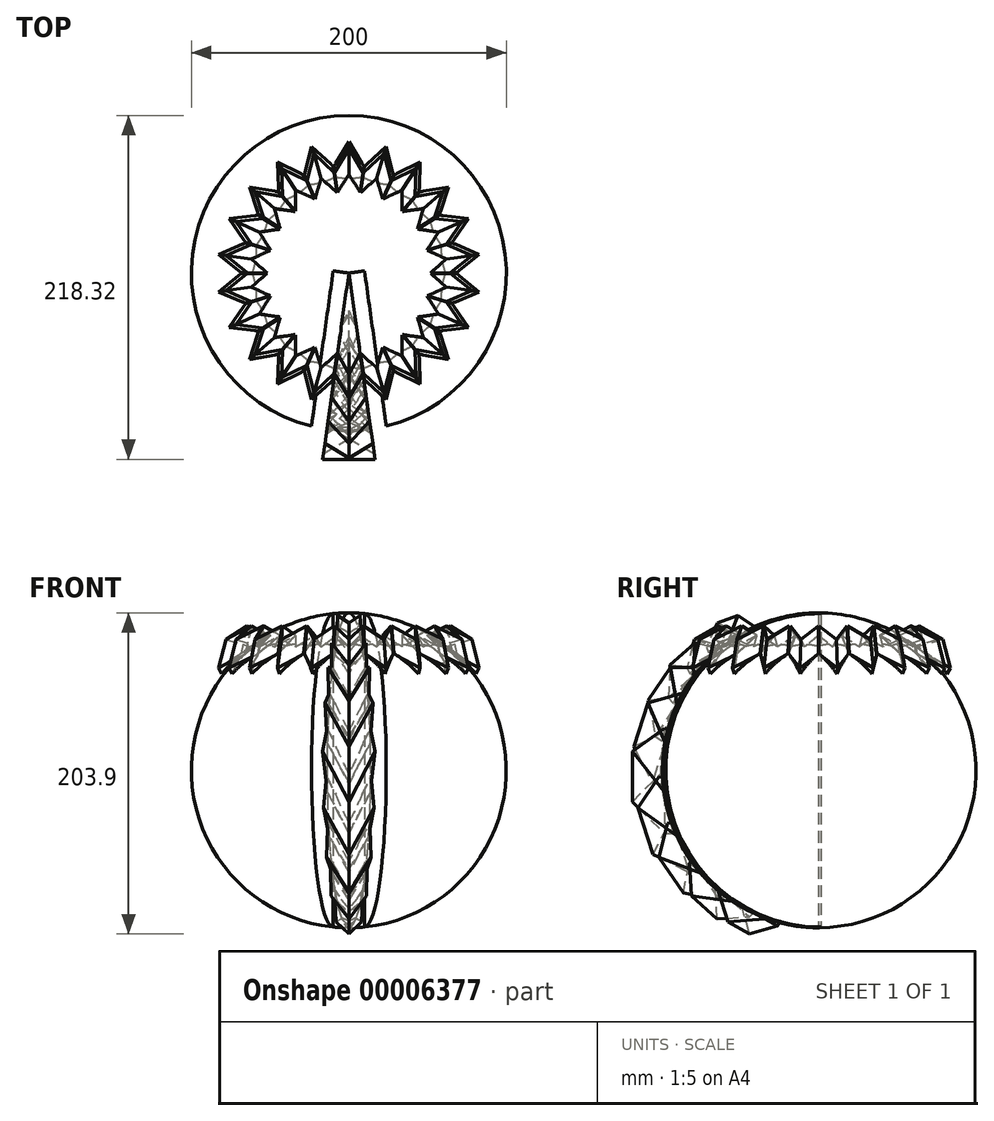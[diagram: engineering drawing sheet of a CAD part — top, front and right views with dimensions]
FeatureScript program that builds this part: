
annotation { "Feature Type Name" : "Feature", "Feature Type Description" : "" }
export const myFeature = defineFeature(function(context is Context, id is Id, definition is map)
    precondition{}
    {
        {
            var Q0;
            Q0=qCreatedBy(makeId("Front.planeOp"),FACE);
            var sketch = newSketch(context, id + "F0", { "sketchPlane" : qUnion([Q0])});
            skLineSegment(sketch, "E0", {"start": v(-20.82, 40) * mm, "end": v(0, 0) * mm});
            skLineSegment(sketch, "E1", {"start": v(0, 0) * mm, "end": v(20.82, 40) * mm});
            skLineSegment(sketch, "E2", {"start": v(-20.82, 40) * mm, "end": v(-20.82, 80) * mm});
            skLineSegment(sketch, "E3", {"start": v(-20.82, 80) * mm, "end": v(0, 40) * mm});
            skLineSegment(sketch, "E4", {"start": v(0, 40) * mm, "end": v(20.82, 80) * mm});
            skLineSegment(sketch, "E5", {"start": v(20.82, 80) * mm, "end": v(20.82, 40) * mm});
            skSolve(sketch);
        }
        {
            var Q0;
            Q0=makeQuery(id+"F0.imprint","IMPRINT",FACE,{"disambiguationData":[TD([[makeQuery(id+"F0.imprint","IMPRINT",EDGE,{"derivedFrom":sQuery(id+"F0.wireOp",EDGE,"E0")}),1.0]])]});
            extrude(context, id + "F1", {"entities" : qUnion([Q0]), "depth" : 120 * mm});
        }
        {
            var Q0;
            Q0=makeQuery(id+"F1.opExtrude","CAP_EDGE",EDGE,{"disambiguationData":[OSD([sQuery(id+"F0.wireOp",EDGE,"E3")])],"isStart":false});
            var Q1;
            Q1=makeQuery(id+"F1.opExtrude","CAP_EDGE",EDGE,{"disambiguationData":[OSD([sQuery(id+"F0.wireOp",EDGE,"E4")])],"isStart":false});
            var Q2;
            Q2=makeQuery(id+"F1.opExtrude","CAP_EDGE",EDGE,{"disambiguationData":[OSD([sQuery(id+"F0.wireOp",EDGE,"E1")])],"isStart":false});
            var Q3;
            Q3=makeQuery(id+"F1.opExtrude","CAP_EDGE",EDGE,{"disambiguationData":[OSD([sQuery(id+"F0.wireOp",EDGE,"E0")])],"isStart":false});
            chamfer(context, id + "F2", {"entities" : qUnion([Q0, Q1, Q2, Q3]), "chamferType" : ChamferType.TWO_OFFSETS, "width1" : 22 * mm, "oppositeDirection" : false, "width2" : 10 * mm, "tangentPropagation" : true});
        }
        {
            var Q0;
            Q0=qCreatedBy(makeId("Right.planeOp"),FACE);
            var sketch = newSketch(context, id + "F3", { "sketchPlane" : qUnion([Q0])});
            skArc(sketch, "E6", {"start": v(0, 140) * mm, "mid": v(-100, 40) * mm, "end": v(0, -60) * mm});
            skLineSegment(sketch, "E7", {"start": v(0, 140) * mm, "end": v(0, -60) * mm});
            skSolve(sketch);
        }
        {
            var Q0;
            Q0=makeQuery(id+"F3.imprint","IMPRINT",FACE,{"disambiguationData":[TD([[makeQuery(id+"F3.imprint","IMPRINT",EDGE,{"derivedFrom":sQuery(id+"F3.wireOp",EDGE,"E6")}),1.0]])]});
            var Q1;
            Q1=sQuery(id+"F3.wireOp",EDGE,"E7");
            revolve(context, id + "F4", {"entities" : qUnion([Q0]), "axis" : qUnion([Q1]), "revolveType" : RevolveType.FULL});
        }
        {
            var Q0;
            Q0=makeQuery(id+"F4.opRevolve","SWEPT_BODY",BODY,{"disambiguationData":[OSD([sQuery(id+"F3.wireOp",EDGE,"E6"),sQuery(id+"F3.wireOp",EDGE,"E7")])]});
            var Q1;
            Q1=makeQuery(id+"F1.opExtrude","SWEPT_BODY",BODY,{"disambiguationData":[OSD([sQuery(id+"F0.wireOp",EDGE,"E0"),sQuery(id+"F0.wireOp",EDGE,"E1"),sQuery(id+"F0.wireOp",EDGE,"E2"),sQuery(id+"F0.wireOp",EDGE,"E3"),sQuery(id+"F0.wireOp",EDGE,"E4"),sQuery(id+"F0.wireOp",EDGE,"E5")])]});
            booleanBodies(context, id + "F5", {"operationType" : BooleanOperationType.SUBTRACTION, "tools" : qUnion([Q0]), "targets" : qUnion([Q1]), "keepTools" : true});
        }
        {
            var Q0;
            Q0=makeQuery(id+"F1.opExtrude","SWEPT_BODY",BODY,{"disambiguationData":[OSD([sQuery(id+"F0.wireOp",EDGE,"E0"),sQuery(id+"F0.wireOp",EDGE,"E1"),sQuery(id+"F0.wireOp",EDGE,"E2"),sQuery(id+"F0.wireOp",EDGE,"E3"),sQuery(id+"F0.wireOp",EDGE,"E4"),sQuery(id+"F0.wireOp",EDGE,"E5")])]});
            var Q1;
            Q1=sQuery(id+"F3.wireOp",EDGE,"E6");
            circularPattern(context, id + "F6", {"entities" : qUnion([Q0]), "axis" : qUnion([Q1]), "angle" : 18 * degree, "instanceCount" : 2, "oppositeDirection" : true});
        }
        {
            var Q0;
            Q0=makeQuery(id+"F1.opExtrude","SWEPT_BODY",BODY,{"disambiguationData":[OSD([sQuery(id+"F0.wireOp",EDGE,"E0"),sQuery(id+"F0.wireOp",EDGE,"E1"),sQuery(id+"F0.wireOp",EDGE,"E2"),sQuery(id+"F0.wireOp",EDGE,"E3"),sQuery(id+"F0.wireOp",EDGE,"E4"),sQuery(id+"F0.wireOp",EDGE,"E5")])]});
            var Q1;
            Q1=sQuery(id+"F3.wireOp",EDGE,"E6");
            circularPattern(context, id + "F7", {"entities" : qUnion([Q0]), "axis" : qUnion([Q1]), "angle" : 18 * degree, "instanceCount" : 2});
        }
        {
            var Q0;
            Q0=makeQuery(id+"F6.opPattern","COPY",BODY,{"derivedFrom":makeQuery(id+"F1.opExtrude","SWEPT_BODY",BODY,{"disambiguationData":[OSD([sQuery(id+"F0.wireOp",EDGE,"E0"),sQuery(id+"F0.wireOp",EDGE,"E1"),sQuery(id+"F0.wireOp",EDGE,"E2"),sQuery(id+"F0.wireOp",EDGE,"E3"),sQuery(id+"F0.wireOp",EDGE,"E4"),sQuery(id+"F0.wireOp",EDGE,"E5")])]}),"instanceName":"1"});
            var Q1;
            {var subQ0=sQuery(id+"F0.wireOp",EDGE,"E0");var subQ1=sQuery(id+"F0.wireOp",EDGE,"E1");Q1=makeQuery(id+"F6.opPattern","COPY",VERTEX,{"derivedFrom":makeQuery(id+"F2.opChamfer","BLEND_VERTEX",VERTEX,{"blendedFrom":[makeQuery(id+"F1.opExtrude","CAP_EDGE",EDGE,{"disambiguationData":[OSD([subQ0])],"isStart":false}),makeQuery(id+"F1.opExtrude","CAP_EDGE",EDGE,{"disambiguationData":[OSD([subQ1])],"isStart":false}),makeQuery(id+"F1.opExtrude","SWEPT_FACE",FACE,{"disambiguationData":[OSD([subQ0])]}),makeQuery(id+"F1.opExtrude","SWEPT_FACE",FACE,{"disambiguationData":[OSD([subQ1])]})],"blendedInto":[makeQuery(id+"F1.opExtrude","SWEPT_FACE",FACE,{"disambiguationData":[OSD([subQ0])]}),makeQuery(id+"F1.opExtrude","SWEPT_FACE",FACE,{"disambiguationData":[OSD([subQ1])]})]}),"instanceName":"1"});}
            transform(context, id + "F8", {"entities" : qUnion([Q0]), "transformType" : TransformType.SCALE_UNIFORMLY, "scale" : .9, "makeCopy" : false, "scalePoint" : qUnion([Q1])});
        }
        {
            var Q0;
            Q0=makeQuery(id+"F7.opPattern","COPY",BODY,{"derivedFrom":makeQuery(id+"F1.opExtrude","SWEPT_BODY",BODY,{"disambiguationData":[OSD([sQuery(id+"F0.wireOp",EDGE,"E0"),sQuery(id+"F0.wireOp",EDGE,"E1"),sQuery(id+"F0.wireOp",EDGE,"E2"),sQuery(id+"F0.wireOp",EDGE,"E3"),sQuery(id+"F0.wireOp",EDGE,"E4"),sQuery(id+"F0.wireOp",EDGE,"E5")])]}),"instanceName":"1"});
            var Q1;
            Q1=makeQuery(id+"F7.opPattern","COPY",VERTEX,{"derivedFrom":makeQuery(id+"F5.opBoolean","INTERSECT",VERTEX,{"derivedFrom":[makeQuery(id+"F2.opChamfer","BLEND_FACE",FACE,{"disambiguationData":[OSD([sQuery(id+"F0.wireOp",EDGE,"E3")])]}),makeQuery(id+"F2.opChamfer","BLEND_FACE",FACE,{"disambiguationData":[OSD([sQuery(id+"F0.wireOp",EDGE,"E4")])]}),makeQuery(id+"F4.opRevolve","SWEPT_FACE",FACE,{"disambiguationData":[OSD([sQuery(id+"F3.wireOp",EDGE,"E6")])]})]}),"instanceName":"1"});
            transform(context, id + "F9", {"entities" : qUnion([Q0]), "transformType" : TransformType.SCALE_UNIFORMLY, "scale" : .9, "makeCopy" : false, "scalePoint" : qUnion([Q1])});
        }
        {
            var Q0;
            Q0=makeQuery(id+"F6.opPattern","COPY",BODY,{"derivedFrom":makeQuery(id+"F1.opExtrude","SWEPT_BODY",BODY,{"disambiguationData":[OSD([sQuery(id+"F0.wireOp",EDGE,"E0"),sQuery(id+"F0.wireOp",EDGE,"E1"),sQuery(id+"F0.wireOp",EDGE,"E2"),sQuery(id+"F0.wireOp",EDGE,"E3"),sQuery(id+"F0.wireOp",EDGE,"E4"),sQuery(id+"F0.wireOp",EDGE,"E5")])]}),"instanceName":"1"});
            var Q1;
            Q1=sQuery(id+"F3.wireOp",EDGE,"E6");
            circularPattern(context, id + "F10", {"entities" : qUnion([Q0]), "axis" : qUnion([Q1]), "angle" : 16 * degree, "instanceCount" : 2, "oppositeDirection" : true});
        }
        {
            var Q0;
            Q0=makeQuery(id+"F7.opPattern","COPY",BODY,{"derivedFrom":makeQuery(id+"F1.opExtrude","SWEPT_BODY",BODY,{"disambiguationData":[OSD([sQuery(id+"F0.wireOp",EDGE,"E0"),sQuery(id+"F0.wireOp",EDGE,"E1"),sQuery(id+"F0.wireOp",EDGE,"E2"),sQuery(id+"F0.wireOp",EDGE,"E3"),sQuery(id+"F0.wireOp",EDGE,"E4"),sQuery(id+"F0.wireOp",EDGE,"E5")])]}),"instanceName":"1"});
            var Q1;
            Q1=sQuery(id+"F3.wireOp",EDGE,"E6");
            circularPattern(context, id + "F11", {"entities" : qUnion([Q0]), "axis" : qUnion([Q1]), "angle" : 16 * degree, "instanceCount" : 2});
        }
        {
            var Q0;
            Q0=makeQuery(id+"F10.opPattern","COPY",BODY,{"derivedFrom":makeQuery(id+"F6.opPattern","COPY",BODY,{"derivedFrom":makeQuery(id+"F1.opExtrude","SWEPT_BODY",BODY,{"disambiguationData":[OSD([sQuery(id+"F0.wireOp",EDGE,"E0"),sQuery(id+"F0.wireOp",EDGE,"E1"),sQuery(id+"F0.wireOp",EDGE,"E2"),sQuery(id+"F0.wireOp",EDGE,"E3"),sQuery(id+"F0.wireOp",EDGE,"E4"),sQuery(id+"F0.wireOp",EDGE,"E5")])]}),"instanceName":"1"}),"instanceName":"1"});
            var Q1;
            {var subQ0=sQuery(id+"F0.wireOp",EDGE,"E0");var subQ1=sQuery(id+"F0.wireOp",EDGE,"E1");Q1=makeQuery(id+"F10.opPattern","COPY",VERTEX,{"derivedFrom":makeQuery(id+"F6.opPattern","COPY",VERTEX,{"derivedFrom":makeQuery(id+"F2.opChamfer","BLEND_VERTEX",VERTEX,{"blendedFrom":[makeQuery(id+"F1.opExtrude","CAP_EDGE",EDGE,{"disambiguationData":[OSD([subQ0])],"isStart":false}),makeQuery(id+"F1.opExtrude","CAP_EDGE",EDGE,{"disambiguationData":[OSD([subQ1])],"isStart":false}),makeQuery(id+"F1.opExtrude","SWEPT_FACE",FACE,{"disambiguationData":[OSD([subQ0])]}),makeQuery(id+"F1.opExtrude","SWEPT_FACE",FACE,{"disambiguationData":[OSD([subQ1])]})],"blendedInto":[makeQuery(id+"F1.opExtrude","SWEPT_FACE",FACE,{"disambiguationData":[OSD([subQ0])]}),makeQuery(id+"F1.opExtrude","SWEPT_FACE",FACE,{"disambiguationData":[OSD([subQ1])]})]}),"instanceName":"1"}),"instanceName":"1"});}
            transform(context, id + "F12", {"entities" : qUnion([Q0]), "transformType" : TransformType.SCALE_UNIFORMLY, "scale" : .9, "makeCopy" : false, "scalePoint" : qUnion([Q1])});
        }
        {
            var Q0;
            Q0=makeQuery(id+"F11.opPattern","COPY",BODY,{"derivedFrom":makeQuery(id+"F7.opPattern","COPY",BODY,{"derivedFrom":makeQuery(id+"F1.opExtrude","SWEPT_BODY",BODY,{"disambiguationData":[OSD([sQuery(id+"F0.wireOp",EDGE,"E0"),sQuery(id+"F0.wireOp",EDGE,"E1"),sQuery(id+"F0.wireOp",EDGE,"E2"),sQuery(id+"F0.wireOp",EDGE,"E3"),sQuery(id+"F0.wireOp",EDGE,"E4"),sQuery(id+"F0.wireOp",EDGE,"E5")])]}),"instanceName":"1"}),"instanceName":"1"});
            var Q1;
            Q1=makeQuery(id+"F11.opPattern","COPY",VERTEX,{"derivedFrom":makeQuery(id+"F7.opPattern","COPY",VERTEX,{"derivedFrom":makeQuery(id+"F5.opBoolean","INTERSECT",VERTEX,{"derivedFrom":[makeQuery(id+"F2.opChamfer","BLEND_FACE",FACE,{"disambiguationData":[OSD([sQuery(id+"F0.wireOp",EDGE,"E3")])]}),makeQuery(id+"F2.opChamfer","BLEND_FACE",FACE,{"disambiguationData":[OSD([sQuery(id+"F0.wireOp",EDGE,"E4")])]}),makeQuery(id+"F4.opRevolve","SWEPT_FACE",FACE,{"disambiguationData":[OSD([sQuery(id+"F3.wireOp",EDGE,"E6")])]})]}),"instanceName":"1"}),"instanceName":"1"});
            transform(context, id + "F13", {"entities" : qUnion([Q0]), "transformType" : TransformType.SCALE_UNIFORMLY, "scale" : .9, "makeCopy" : false, "scalePoint" : qUnion([Q1])});
        }
        {
            var Q0;
            Q0=makeQuery(id+"F10.opPattern","COPY",BODY,{"derivedFrom":makeQuery(id+"F6.opPattern","COPY",BODY,{"derivedFrom":makeQuery(id+"F1.opExtrude","SWEPT_BODY",BODY,{"disambiguationData":[OSD([sQuery(id+"F0.wireOp",EDGE,"E0"),sQuery(id+"F0.wireOp",EDGE,"E1"),sQuery(id+"F0.wireOp",EDGE,"E2"),sQuery(id+"F0.wireOp",EDGE,"E3"),sQuery(id+"F0.wireOp",EDGE,"E4"),sQuery(id+"F0.wireOp",EDGE,"E5")])]}),"instanceName":"1"}),"instanceName":"1"});
            var Q1;
            Q1=sQuery(id+"F3.wireOp",EDGE,"E6");
            circularPattern(context, id + "F14", {"entities" : qUnion([Q0]), "axis" : qUnion([Q1]), "angle" : 14 * degree, "instanceCount" : 2, "oppositeDirection" : true});
        }
        {
            var Q0;
            Q0=makeQuery(id+"F11.opPattern","COPY",BODY,{"derivedFrom":makeQuery(id+"F7.opPattern","COPY",BODY,{"derivedFrom":makeQuery(id+"F1.opExtrude","SWEPT_BODY",BODY,{"disambiguationData":[OSD([sQuery(id+"F0.wireOp",EDGE,"E0"),sQuery(id+"F0.wireOp",EDGE,"E1"),sQuery(id+"F0.wireOp",EDGE,"E2"),sQuery(id+"F0.wireOp",EDGE,"E3"),sQuery(id+"F0.wireOp",EDGE,"E4"),sQuery(id+"F0.wireOp",EDGE,"E5")])]}),"instanceName":"1"}),"instanceName":"1"});
            var Q1;
            Q1=sQuery(id+"F3.wireOp",EDGE,"E6");
            circularPattern(context, id + "F15", {"entities" : qUnion([Q0]), "axis" : qUnion([Q1]), "angle" : 14 * degree, "instanceCount" : 2});
        }
        {
            var Q0;
            Q0=makeQuery(id+"F14.opPattern","COPY",BODY,{"derivedFrom":makeQuery(id+"F10.opPattern","COPY",BODY,{"derivedFrom":makeQuery(id+"F6.opPattern","COPY",BODY,{"derivedFrom":makeQuery(id+"F1.opExtrude","SWEPT_BODY",BODY,{"disambiguationData":[OSD([sQuery(id+"F0.wireOp",EDGE,"E0"),sQuery(id+"F0.wireOp",EDGE,"E1"),sQuery(id+"F0.wireOp",EDGE,"E2"),sQuery(id+"F0.wireOp",EDGE,"E3"),sQuery(id+"F0.wireOp",EDGE,"E4"),sQuery(id+"F0.wireOp",EDGE,"E5")])]}),"instanceName":"1"}),"instanceName":"1"}),"instanceName":"1"});
            var Q1;
            {var subQ0=sQuery(id+"F0.wireOp",EDGE,"E0");var subQ1=sQuery(id+"F0.wireOp",EDGE,"E1");Q1=makeQuery(id+"F14.opPattern","COPY",VERTEX,{"derivedFrom":makeQuery(id+"F10.opPattern","COPY",VERTEX,{"derivedFrom":makeQuery(id+"F6.opPattern","COPY",VERTEX,{"derivedFrom":makeQuery(id+"F2.opChamfer","BLEND_VERTEX",VERTEX,{"blendedFrom":[makeQuery(id+"F1.opExtrude","CAP_EDGE",EDGE,{"disambiguationData":[OSD([subQ0])],"isStart":false}),makeQuery(id+"F1.opExtrude","CAP_EDGE",EDGE,{"disambiguationData":[OSD([subQ1])],"isStart":false}),makeQuery(id+"F1.opExtrude","SWEPT_FACE",FACE,{"disambiguationData":[OSD([subQ0])]}),makeQuery(id+"F1.opExtrude","SWEPT_FACE",FACE,{"disambiguationData":[OSD([subQ1])]})],"blendedInto":[makeQuery(id+"F1.opExtrude","SWEPT_FACE",FACE,{"disambiguationData":[OSD([subQ0])]}),makeQuery(id+"F1.opExtrude","SWEPT_FACE",FACE,{"disambiguationData":[OSD([subQ1])]})]}),"instanceName":"1"}),"instanceName":"1"}),"instanceName":"1"});}
            transform(context, id + "F16", {"entities" : qUnion([Q0]), "transformType" : TransformType.SCALE_UNIFORMLY, "scale" : .9, "makeCopy" : false, "scalePoint" : qUnion([Q1])});
        }
        {
            var Q0;
            Q0=makeQuery(id+"F15.opPattern","COPY",BODY,{"derivedFrom":makeQuery(id+"F11.opPattern","COPY",BODY,{"derivedFrom":makeQuery(id+"F7.opPattern","COPY",BODY,{"derivedFrom":makeQuery(id+"F1.opExtrude","SWEPT_BODY",BODY,{"disambiguationData":[OSD([sQuery(id+"F0.wireOp",EDGE,"E0"),sQuery(id+"F0.wireOp",EDGE,"E1"),sQuery(id+"F0.wireOp",EDGE,"E2"),sQuery(id+"F0.wireOp",EDGE,"E3"),sQuery(id+"F0.wireOp",EDGE,"E4"),sQuery(id+"F0.wireOp",EDGE,"E5")])]}),"instanceName":"1"}),"instanceName":"1"}),"instanceName":"1"});
            var Q1;
            Q1=makeQuery(id+"F15.opPattern","COPY",VERTEX,{"derivedFrom":makeQuery(id+"F11.opPattern","COPY",VERTEX,{"derivedFrom":makeQuery(id+"F7.opPattern","COPY",VERTEX,{"derivedFrom":makeQuery(id+"F5.opBoolean","INTERSECT",VERTEX,{"derivedFrom":[makeQuery(id+"F2.opChamfer","BLEND_FACE",FACE,{"disambiguationData":[OSD([sQuery(id+"F0.wireOp",EDGE,"E3")])]}),makeQuery(id+"F2.opChamfer","BLEND_FACE",FACE,{"disambiguationData":[OSD([sQuery(id+"F0.wireOp",EDGE,"E4")])]}),makeQuery(id+"F4.opRevolve","SWEPT_FACE",FACE,{"disambiguationData":[OSD([sQuery(id+"F3.wireOp",EDGE,"E6")])]})]}),"instanceName":"1"}),"instanceName":"1"}),"instanceName":"1"});
            transform(context, id + "F17", {"entities" : qUnion([Q0]), "transformType" : TransformType.SCALE_UNIFORMLY, "scale" : .9, "makeCopy" : false, "scalePoint" : qUnion([Q1])});
        }
        {
            var Q0;
            Q0=makeQuery(id+"F14.opPattern","COPY",BODY,{"derivedFrom":makeQuery(id+"F10.opPattern","COPY",BODY,{"derivedFrom":makeQuery(id+"F6.opPattern","COPY",BODY,{"derivedFrom":makeQuery(id+"F1.opExtrude","SWEPT_BODY",BODY,{"disambiguationData":[OSD([sQuery(id+"F0.wireOp",EDGE,"E0"),sQuery(id+"F0.wireOp",EDGE,"E1"),sQuery(id+"F0.wireOp",EDGE,"E2"),sQuery(id+"F0.wireOp",EDGE,"E3"),sQuery(id+"F0.wireOp",EDGE,"E4"),sQuery(id+"F0.wireOp",EDGE,"E5")])]}),"instanceName":"1"}),"instanceName":"1"}),"instanceName":"1"});
            var Q1;
            Q1=sQuery(id+"F3.wireOp",EDGE,"E6");
            circularPattern(context, id + "F18", {"entities" : qUnion([Q0]), "axis" : qUnion([Q1]), "angle" : 12 * degree, "instanceCount" : 2, "oppositeDirection" : true});
        }
        {
            var Q0;
            Q0=makeQuery(id+"F18.opPattern","COPY",BODY,{"derivedFrom":makeQuery(id+"F14.opPattern","COPY",BODY,{"derivedFrom":makeQuery(id+"F10.opPattern","COPY",BODY,{"derivedFrom":makeQuery(id+"F6.opPattern","COPY",BODY,{"derivedFrom":makeQuery(id+"F1.opExtrude","SWEPT_BODY",BODY,{"disambiguationData":[OSD([sQuery(id+"F0.wireOp",EDGE,"E0"),sQuery(id+"F0.wireOp",EDGE,"E1"),sQuery(id+"F0.wireOp",EDGE,"E2"),sQuery(id+"F0.wireOp",EDGE,"E3"),sQuery(id+"F0.wireOp",EDGE,"E4"),sQuery(id+"F0.wireOp",EDGE,"E5")])]}),"instanceName":"1"}),"instanceName":"1"}),"instanceName":"1"}),"instanceName":"1"});
            var Q1;
            {var subQ0=sQuery(id+"F0.wireOp",EDGE,"E0");var subQ1=sQuery(id+"F0.wireOp",EDGE,"E1");Q1=makeQuery(id+"F18.opPattern","COPY",VERTEX,{"derivedFrom":makeQuery(id+"F14.opPattern","COPY",VERTEX,{"derivedFrom":makeQuery(id+"F10.opPattern","COPY",VERTEX,{"derivedFrom":makeQuery(id+"F6.opPattern","COPY",VERTEX,{"derivedFrom":makeQuery(id+"F2.opChamfer","BLEND_VERTEX",VERTEX,{"blendedFrom":[makeQuery(id+"F1.opExtrude","CAP_EDGE",EDGE,{"disambiguationData":[OSD([subQ0])],"isStart":false}),makeQuery(id+"F1.opExtrude","CAP_EDGE",EDGE,{"disambiguationData":[OSD([subQ1])],"isStart":false}),makeQuery(id+"F1.opExtrude","SWEPT_FACE",FACE,{"disambiguationData":[OSD([subQ0])]}),makeQuery(id+"F1.opExtrude","SWEPT_FACE",FACE,{"disambiguationData":[OSD([subQ1])]})],"blendedInto":[makeQuery(id+"F1.opExtrude","SWEPT_FACE",FACE,{"disambiguationData":[OSD([subQ0])]}),makeQuery(id+"F1.opExtrude","SWEPT_FACE",FACE,{"disambiguationData":[OSD([subQ1])]})]}),"instanceName":"1"}),"instanceName":"1"}),"instanceName":"1"}),"instanceName":"1"});}
            transform(context, id + "F19", {"entities" : qUnion([Q0]), "transformType" : TransformType.SCALE_UNIFORMLY, "scale" : .9, "makeCopy" : false, "scalePoint" : qUnion([Q1])});
        }
        {
            var Q0;
            Q0=makeQuery(id+"F15.opPattern","COPY",BODY,{"derivedFrom":makeQuery(id+"F11.opPattern","COPY",BODY,{"derivedFrom":makeQuery(id+"F7.opPattern","COPY",BODY,{"derivedFrom":makeQuery(id+"F1.opExtrude","SWEPT_BODY",BODY,{"disambiguationData":[OSD([sQuery(id+"F0.wireOp",EDGE,"E0"),sQuery(id+"F0.wireOp",EDGE,"E1"),sQuery(id+"F0.wireOp",EDGE,"E2"),sQuery(id+"F0.wireOp",EDGE,"E3"),sQuery(id+"F0.wireOp",EDGE,"E4"),sQuery(id+"F0.wireOp",EDGE,"E5")])]}),"instanceName":"1"}),"instanceName":"1"}),"instanceName":"1"});
            var Q1;
            Q1=sQuery(id+"F3.wireOp",EDGE,"E6");
            circularPattern(context, id + "F20", {"entities" : qUnion([Q0]), "axis" : qUnion([Q1]), "angle" : 12 * degree, "instanceCount" : 2});
        }
        {
            var Q0;
            Q0=makeQuery(id+"F20.opPattern","COPY",BODY,{"derivedFrom":makeQuery(id+"F15.opPattern","COPY",BODY,{"derivedFrom":makeQuery(id+"F11.opPattern","COPY",BODY,{"derivedFrom":makeQuery(id+"F7.opPattern","COPY",BODY,{"derivedFrom":makeQuery(id+"F1.opExtrude","SWEPT_BODY",BODY,{"disambiguationData":[OSD([sQuery(id+"F0.wireOp",EDGE,"E0"),sQuery(id+"F0.wireOp",EDGE,"E1"),sQuery(id+"F0.wireOp",EDGE,"E2"),sQuery(id+"F0.wireOp",EDGE,"E3"),sQuery(id+"F0.wireOp",EDGE,"E4"),sQuery(id+"F0.wireOp",EDGE,"E5")])]}),"instanceName":"1"}),"instanceName":"1"}),"instanceName":"1"}),"instanceName":"1"});
            var Q1;
            Q1=makeQuery(id+"F20.opPattern","COPY",VERTEX,{"derivedFrom":makeQuery(id+"F15.opPattern","COPY",VERTEX,{"derivedFrom":makeQuery(id+"F11.opPattern","COPY",VERTEX,{"derivedFrom":makeQuery(id+"F7.opPattern","COPY",VERTEX,{"derivedFrom":makeQuery(id+"F5.opBoolean","INTERSECT",VERTEX,{"derivedFrom":[makeQuery(id+"F2.opChamfer","BLEND_FACE",FACE,{"disambiguationData":[OSD([sQuery(id+"F0.wireOp",EDGE,"E3")])]}),makeQuery(id+"F2.opChamfer","BLEND_FACE",FACE,{"disambiguationData":[OSD([sQuery(id+"F0.wireOp",EDGE,"E4")])]}),makeQuery(id+"F4.opRevolve","SWEPT_FACE",FACE,{"disambiguationData":[OSD([sQuery(id+"F3.wireOp",EDGE,"E6")])]})]}),"instanceName":"1"}),"instanceName":"1"}),"instanceName":"1"}),"instanceName":"1"});
            transform(context, id + "F21", {"entities" : qUnion([Q0]), "transformType" : TransformType.SCALE_UNIFORMLY, "scale" : .9, "makeCopy" : false, "scalePoint" : qUnion([Q1])});
        }
        {
            var Q0;
            Q0=makeQuery(id+"F18.opPattern","COPY",BODY,{"derivedFrom":makeQuery(id+"F14.opPattern","COPY",BODY,{"derivedFrom":makeQuery(id+"F10.opPattern","COPY",BODY,{"derivedFrom":makeQuery(id+"F6.opPattern","COPY",BODY,{"derivedFrom":makeQuery(id+"F1.opExtrude","SWEPT_BODY",BODY,{"disambiguationData":[OSD([sQuery(id+"F0.wireOp",EDGE,"E0"),sQuery(id+"F0.wireOp",EDGE,"E1"),sQuery(id+"F0.wireOp",EDGE,"E2"),sQuery(id+"F0.wireOp",EDGE,"E3"),sQuery(id+"F0.wireOp",EDGE,"E4"),sQuery(id+"F0.wireOp",EDGE,"E5")])]}),"instanceName":"1"}),"instanceName":"1"}),"instanceName":"1"}),"instanceName":"1"});
            var Q1;
            Q1=sQuery(id+"F3.wireOp",EDGE,"E6");
            circularPattern(context, id + "F22", {"entities" : qUnion([Q0]), "axis" : qUnion([Q1]), "angle" : 10 * degree, "instanceCount" : 2, "oppositeDirection" : true});
        }
        {
            var Q0;
            Q0=makeQuery(id+"F22.opPattern","COPY",BODY,{"derivedFrom":makeQuery(id+"F18.opPattern","COPY",BODY,{"derivedFrom":makeQuery(id+"F14.opPattern","COPY",BODY,{"derivedFrom":makeQuery(id+"F10.opPattern","COPY",BODY,{"derivedFrom":makeQuery(id+"F6.opPattern","COPY",BODY,{"derivedFrom":makeQuery(id+"F1.opExtrude","SWEPT_BODY",BODY,{"disambiguationData":[OSD([sQuery(id+"F0.wireOp",EDGE,"E0"),sQuery(id+"F0.wireOp",EDGE,"E1"),sQuery(id+"F0.wireOp",EDGE,"E2"),sQuery(id+"F0.wireOp",EDGE,"E3"),sQuery(id+"F0.wireOp",EDGE,"E4"),sQuery(id+"F0.wireOp",EDGE,"E5")])]}),"instanceName":"1"}),"instanceName":"1"}),"instanceName":"1"}),"instanceName":"1"}),"instanceName":"1"});
            var Q1;
            {var subQ0=sQuery(id+"F0.wireOp",EDGE,"E0");var subQ1=sQuery(id+"F0.wireOp",EDGE,"E1");Q1=makeQuery(id+"F22.opPattern","COPY",VERTEX,{"derivedFrom":makeQuery(id+"F18.opPattern","COPY",VERTEX,{"derivedFrom":makeQuery(id+"F14.opPattern","COPY",VERTEX,{"derivedFrom":makeQuery(id+"F10.opPattern","COPY",VERTEX,{"derivedFrom":makeQuery(id+"F6.opPattern","COPY",VERTEX,{"derivedFrom":makeQuery(id+"F2.opChamfer","BLEND_VERTEX",VERTEX,{"blendedFrom":[makeQuery(id+"F1.opExtrude","CAP_EDGE",EDGE,{"disambiguationData":[OSD([subQ0])],"isStart":false}),makeQuery(id+"F1.opExtrude","CAP_EDGE",EDGE,{"disambiguationData":[OSD([subQ1])],"isStart":false}),makeQuery(id+"F1.opExtrude","SWEPT_FACE",FACE,{"disambiguationData":[OSD([subQ0])]}),makeQuery(id+"F1.opExtrude","SWEPT_FACE",FACE,{"disambiguationData":[OSD([subQ1])]})],"blendedInto":[makeQuery(id+"F1.opExtrude","SWEPT_FACE",FACE,{"disambiguationData":[OSD([subQ0])]}),makeQuery(id+"F1.opExtrude","SWEPT_FACE",FACE,{"disambiguationData":[OSD([subQ1])]})]}),"instanceName":"1"}),"instanceName":"1"}),"instanceName":"1"}),"instanceName":"1"}),"instanceName":"1"});}
            transform(context, id + "F23", {"entities" : qUnion([Q0]), "transformType" : TransformType.SCALE_UNIFORMLY, "scale" : .9, "makeCopy" : false, "scalePoint" : qUnion([Q1])});
        }
        {
            var Q0;
            Q0=qCreatedBy(makeId("Top.planeOp"),FACE);
            cPlane(context, id + "F24", {"entities" : qUnion([Q0]), "cplaneType" : CPlaneType.OFFSET, "offset" : 40 * mm, "width" : 150 * mm, "height" : 150 * mm});
        }
        {
            var Q0;
            Q0=qCreatedBy(id+"F24.planeOp",FACE);
            var sketch = newSketch(context, id + "F25", { "sketchPlane" : qUnion([Q0])});
            skCircle(sketch, "E8", {"center": v(0, 0) * mm, "radius": 100 * mm});
            skSolve(sketch);
        }
        {
            var Q0;
            Q0=makeQuery(id+"F4.opRevolve","SWEPT_BODY",BODY,{"disambiguationData":[OSD([sQuery(id+"F3.wireOp",EDGE,"E6"),sQuery(id+"F3.wireOp",EDGE,"E7")])]});
            var Q1;
            Q1=makeQuery(id+"F18.opPattern","COPY",BODY,{"derivedFrom":makeQuery(id+"F14.opPattern","COPY",BODY,{"derivedFrom":makeQuery(id+"F10.opPattern","COPY",BODY,{"derivedFrom":makeQuery(id+"F6.opPattern","COPY",BODY,{"derivedFrom":makeQuery(id+"F1.opExtrude","SWEPT_BODY",BODY,{"disambiguationData":[OSD([sQuery(id+"F0.wireOp",EDGE,"E0"),sQuery(id+"F0.wireOp",EDGE,"E1"),sQuery(id+"F0.wireOp",EDGE,"E2"),sQuery(id+"F0.wireOp",EDGE,"E3"),sQuery(id+"F0.wireOp",EDGE,"E4"),sQuery(id+"F0.wireOp",EDGE,"E5")])]}),"instanceName":"1"}),"instanceName":"1"}),"instanceName":"1"}),"instanceName":"1"});
            booleanBodies(context, id + "F26", {"operationType" : BooleanOperationType.SUBTRACTION, "tools" : qUnion([Q0]), "targets" : qUnion([Q1]), "keepTools" : true});
        }
        {
            var Q0;
            Q0=sQuery(id+"F3.wireOp",EDGE,"E7");
            cPlane(context, id + "F27", {"entities" : qUnion([Q0]), "cplaneType" : CPlaneType.LINE_ANGLE, "offset" : 150 * mm, "angle" : 12 * degree, "width" : 150 * mm, "height" : 150 * mm});
        }
        {
            var Q0;
            Q0=sQuery(id+"F3.wireOp",EDGE,"E7");
            cPlane(context, id + "F28", {"entities" : qUnion([Q0]), "cplaneType" : CPlaneType.LINE_ANGLE, "offset" : 150 * mm, "angle" : 348 * degree, "width" : 150 * mm, "height" : 150 * mm});
        }
        {
            var Q0;
            Q0=qCreatedBy(id+"F28.planeOp",FACE);
            var sketch = newSketch(context, id + "F29", { "sketchPlane" : qUnion([Q0])});
            skCircle(sketch, "E9", {"center": v(0, 40) * mm, "radius": 100 * mm});
            skSolve(sketch);
        }
        {
            var Q0;
            Q0=sQuery(id+"F3.wireOp",EDGE,"E7");
            cPlane(context, id + "F30", {"entities" : qUnion([Q0]), "cplaneType" : CPlaneType.LINE_ANGLE, "offset" : 150 * mm, "angle" : 98 * degree, "width" : 150 * mm, "height" : 150 * mm});
        }
        {
            var Q0;
            Q0=sQuery(id+"F3.wireOp",EDGE,"E7");
            cPlane(context, id + "F31", {"entities" : qUnion([Q0]), "cplaneType" : CPlaneType.LINE_ANGLE, "offset" : 150 * mm, "angle" : 262 * degree, "width" : 150 * mm, "height" : 150 * mm});
        }
        {
            var Q0;
            Q0=qCreatedBy(id+"F31.planeOp",FACE);
            var sketch = newSketch(context, id + "F32", { "sketchPlane" : qUnion([Q0])});
            skLineSegment(sketch, "E10.0", {"start": v(0, -60) * mm, "end": v(0, 140) * mm});
            skLineSegment(sketch, "E11", {"start": v(0, 140) * mm, "end": v(0, 145) * mm});
            skLineSegment(sketch, "E12", {"start": v(0, 145) * mm, "end": v(10, 145) * mm});
            skLineSegment(sketch, "E13", {"start": v(10, 145) * mm, "end": v(10, -60) * mm});
            skLineSegment(sketch, "E14", {"start": v(10, -60) * mm, "end": v(0, -60) * mm});
            skSolve(sketch);
        }
        {
            var Q0;
            Q0=qCreatedBy(id+"F30.planeOp",FACE);
            var sketch = newSketch(context, id + "F33", { "sketchPlane" : qUnion([Q0])});
            skLineSegment(sketch, "E15.0", {"start": v(0, 140) * mm, "end": v(0, -60) * mm});
            skLineSegment(sketch, "E16.bottom", {"start": v(0, 145) * mm, "end": v(10, 145) * mm});
            skLineSegment(sketch, "E16.top", {"start": v(0, -60) * mm, "end": v(10, -60) * mm});
            skLineSegment(sketch, "E16.left", {"start": v(0, 145) * mm, "end": v(0, -60) * mm});
            skLineSegment(sketch, "E16.right", {"start": v(10, 145) * mm, "end": v(10, -60) * mm});
            skSolve(sketch);
        }
        {
            var Q0;
            {var subQ2=sQuery(id+"F33.wireOp",EDGE,"E16.bottom");Q0=makeQuery(id+"F33.imprint","IMPRINT",FACE,{"disambiguationData":[TD([[makeQuery(id+"F33.imprint","IMPRINT",EDGE,{"derivedFrom":subQ2}),-1.0]])]});}
            extrude(context, id + "F34", {"entities" : qUnion([Q0]), "operationType" : NewBodyOperationType.REMOVE, "endBound" : BoundingType.THROUGH_ALL, "oppositeDirection" : true, "depth" : 25 * mm});
        }
        {
            var Q0;
            Q0=makeQuery(id+"F32.imprint","IMPRINT",FACE,{"disambiguationData":[TD([[makeQuery(id+"F32.imprint","IMPRINT",EDGE,{"derivedFrom":sQuery(id+"F32.wireOp",EDGE,"E10.0")}),-1.0]])]});
            extrude(context, id + "F35", {"entities" : qUnion([Q0]), "operationType" : NewBodyOperationType.REMOVE, "endBound" : BoundingType.THROUGH_ALL, "depth" : 25 * mm});
        }
        {
            var Q0;
            Q0=makeQuery(id+"F18.opPattern","COPY",BODY,{"derivedFrom":makeQuery(id+"F14.opPattern","COPY",BODY,{"derivedFrom":makeQuery(id+"F10.opPattern","COPY",BODY,{"derivedFrom":makeQuery(id+"F6.opPattern","COPY",BODY,{"derivedFrom":makeQuery(id+"F1.opExtrude","SWEPT_BODY",BODY,{"disambiguationData":[OSD([sQuery(id+"F0.wireOp",EDGE,"E0"),sQuery(id+"F0.wireOp",EDGE,"E1"),sQuery(id+"F0.wireOp",EDGE,"E2"),sQuery(id+"F0.wireOp",EDGE,"E3"),sQuery(id+"F0.wireOp",EDGE,"E4"),sQuery(id+"F0.wireOp",EDGE,"E5")])]}),"instanceName":"1"}),"instanceName":"1"}),"instanceName":"1"}),"instanceName":"1"});
            var Q1;
            Q1=sQuery(id+"F25.wireOp",EDGE,"E8");
            circularPattern(context, id + "F36", {"entities" : qUnion([Q0]), "axis" : qUnion([Q1]), "angle" : 360 * degree, "instanceCount" : 22, "equalSpace" : true});
        }
    });
